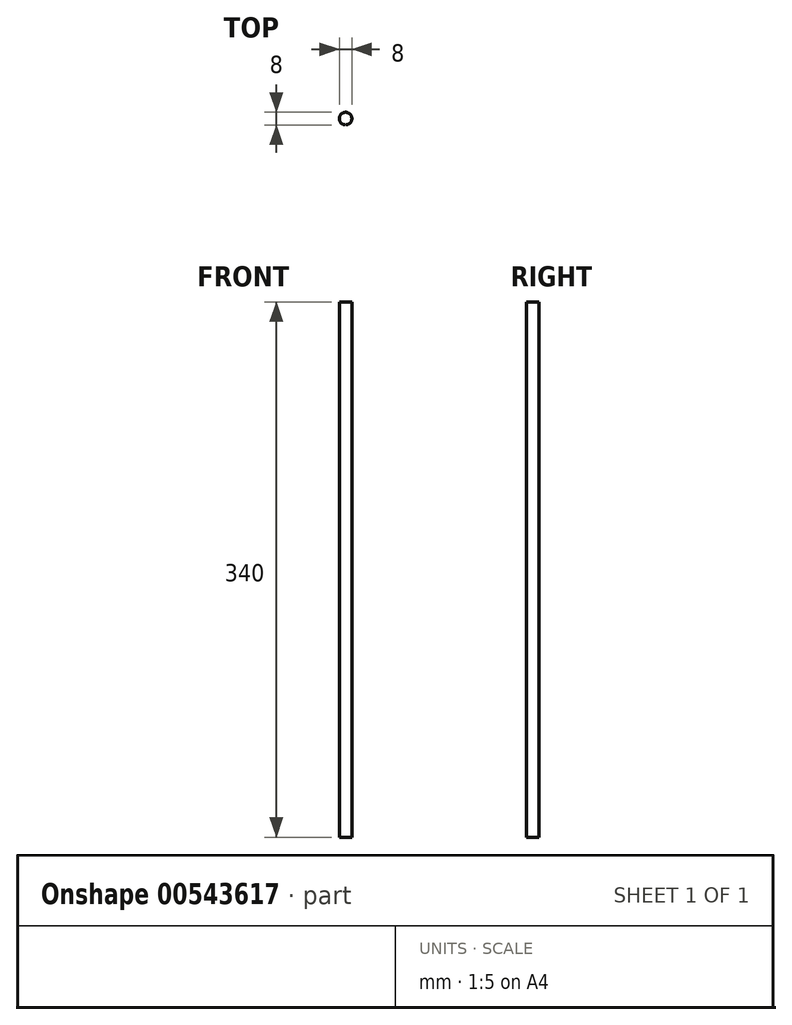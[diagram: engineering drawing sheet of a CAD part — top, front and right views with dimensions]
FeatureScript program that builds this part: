
annotation { "Feature Type Name" : "Feature", "Feature Type Description" : "" }
export const myFeature = defineFeature(function(context is Context, id is Id, definition is map)
    precondition{}
    {
        {
            var Q0;
            Q0=qCreatedBy(makeId("Top.planeOp"),FACE);
            var sketch = newSketch(context, id + "F0", { "sketchPlane" : qUnion([Q0])});
            skCircle(sketch, "E0", {"center": v(0, 0) * mm, "radius": 4 * mm});
            skSolve(sketch);
        }
        {
            var Q0;
            Q0=qSketchRegion(id+"F0",true);
            extrude(context, id + "F1", {"entities" : qUnion([Q0]), "depth" : 340 * mm, "offsetDistance" : 25 * mm});
        }
    });
